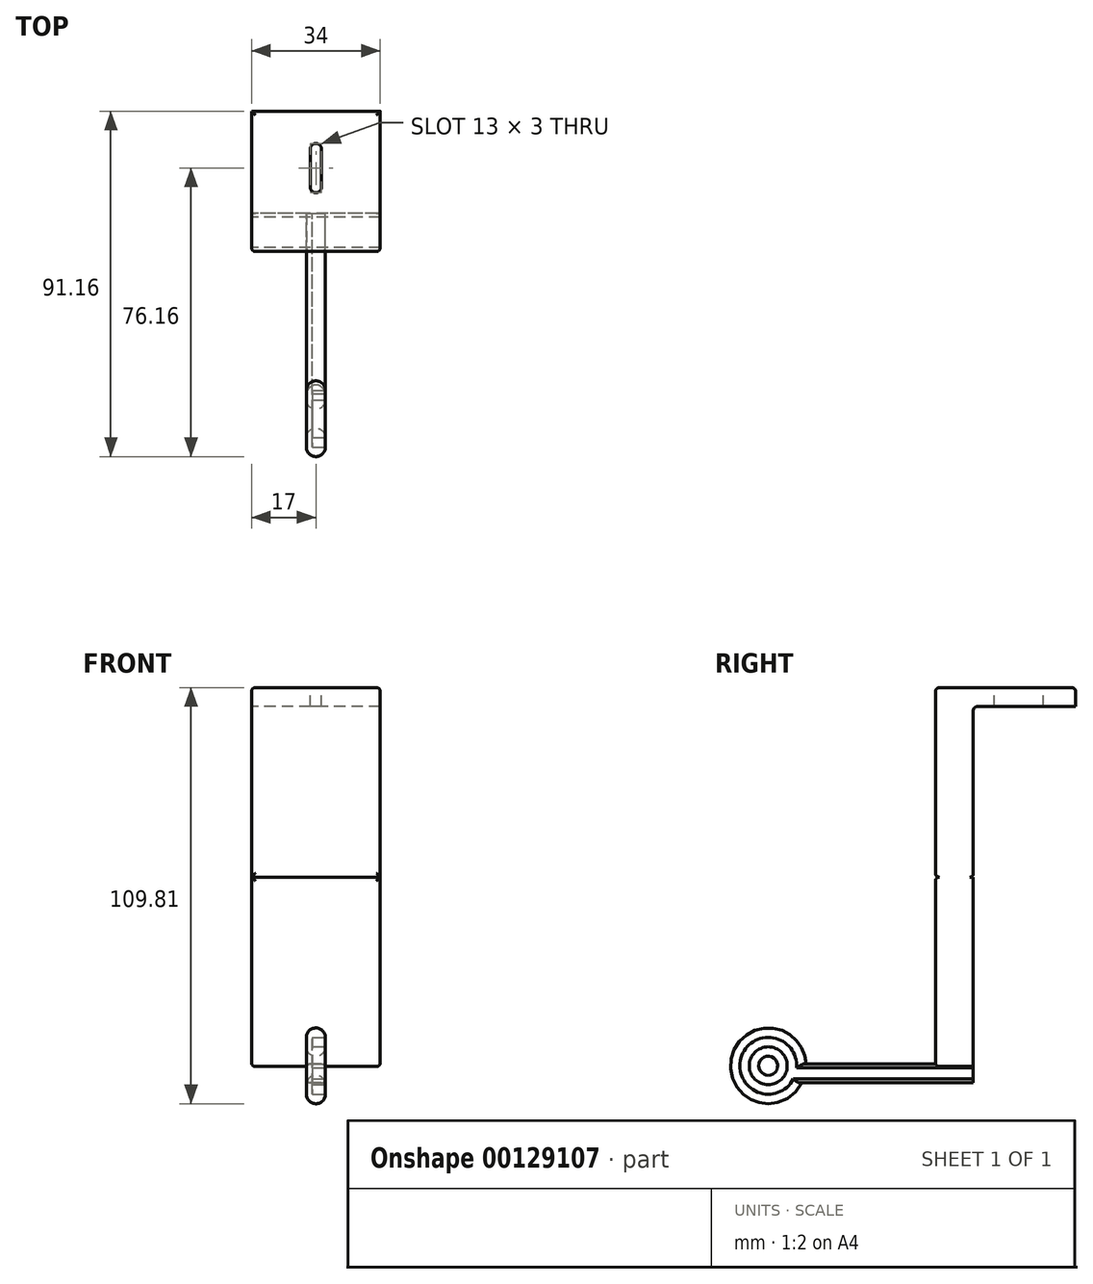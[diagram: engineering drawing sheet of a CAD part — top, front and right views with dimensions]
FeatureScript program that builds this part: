
annotation { "Feature Type Name" : "Feature", "Feature Type Description" : "" }
export const myFeature = defineFeature(function(context is Context, id is Id, definition is map)
    precondition{}
    {
        {
            var Q0;
            Q0=qCreatedBy(makeId("Right.planeOp"),FACE);
            var sketch = newSketch(context, id + "F0", { "sketchPlane" : qUnion([Q0])});
            skLineSegment(sketch, "E0", {"start": v(0, 50) * mm, "end": v(0, 0) * mm});
            skLineSegment(sketch, "E1", {"start": v(0, 0) * mm, "end": v(-10, 0) * mm});
            skLineSegment(sketch, "E2", {"start": v(-10, 0) * mm, "end": v(-10, 45) * mm});
            skLineSegment(sketch, "E3", {"start": v(0, 50) * mm, "end": v(27, 50) * mm});
            skLineSegment(sketch, "E4", {"start": v(27, 50) * mm, "end": v(27, 45) * mm});
            skLineSegment(sketch, "E5", {"start": v(27, 45) * mm, "end": v(0, 45) * mm});
            skLineSegment(sketch, "E6", {"start": v(-10, 45) * mm, "end": v(-10, 50) * mm});
            skLineSegment(sketch, "E7", {"start": v(0, 50) * mm, "end": v(-10, 50) * mm});
            skSolve(sketch);
        }
        {
            var Q0;
            Q0 = qSketchRegion(id + "F0", true);
            extrude(context, id + "F1", {"entities" : qUnion([Q0]), "endBound" : BoundingType.SYMMETRIC, "depth" : 34 * mm});
        }
        {
            var Q0;
            Q0=makeQuery(id+"F1.opExtrude","CAP_EDGE",EDGE,{"disambiguationData":[OSD([sQuery(id+"F0.wireOp",EDGE,"kGD8HcLu-JmXt-PA5V-rn9M-nTJb1uLwhhb4")])],"isStart":true});
            var Q1;
            Q1=makeQuery(id+"F1.opExtrude","SWEPT_EDGE",EDGE,{"disambiguationData":[OSD([sQuery(id+"F0.wireOp",EDGE,"kGD8HcLu-JmXt-PA5V-rn9M-nTJb1uLwhhb4"),sQuery(id+"F0.wireOp",EDGE,"E0")])]});
            var Q2;
            Q2=makeQuery(id+"F1.opExtrude","CAP_EDGE",EDGE,{"disambiguationData":[OSD([sQuery(id+"F0.wireOp",EDGE,"kGD8HcLu-JmXt-PA5V-rn9M-nTJb1uLwhhb4")])],"isStart":false});
            var Q3;
            Q3=makeQuery(id+"F1.opExtrude","SWEPT_EDGE",EDGE,{"disambiguationData":[OSD([sQuery(id+"F0.wireOp",EDGE,"kGD8HcLu-JmXt-PA5V-rn9M-nTJb1uLwhhb4"),sQuery(id+"F0.wireOp",EDGE,"xnDH0qCi-kUXw-gPrd-kgDC-GyTHQjH4Tpmb")])]});
            var Q4;
            Q4=makeQuery(id+"F1.opExtrude","SWEPT_EDGE",EDGE,{"disambiguationData":[OSD([sQuery(id+"F0.wireOp",EDGE,"dkW7WdI2-pFLL-zcu9-3AvS-6kcVhIOYi34H"),sQuery(id+"F0.wireOp",EDGE,"xnDH0qCi-kUXw-gPrd-kgDC-GyTHQjH4Tpmb")])]});
            var Q5;
            Q5=makeQuery(id+"F1.opExtrude","CAP_EDGE",EDGE,{"disambiguationData":[OSD([sQuery(id+"F0.wireOp",EDGE,"xnDH0qCi-kUXw-gPrd-kgDC-GyTHQjH4Tpmb")])],"isStart":false});
            var Q6;
            Q6=makeQuery(id+"F1.opExtrude","CAP_EDGE",EDGE,{"disambiguationData":[OSD([sQuery(id+"F0.wireOp",EDGE,"xnDH0qCi-kUXw-gPrd-kgDC-GyTHQjH4Tpmb")])],"isStart":true});
            var Q7;
            Q7=makeQuery(id+"F1.opExtrude","CAP_EDGE",EDGE,{"disambiguationData":[OSD([sQuery(id+"F0.wireOp",EDGE,"E2")])],"isStart":true});
            var Q8;
            Q8=makeQuery(id+"F1.opExtrude","CAP_EDGE",EDGE,{"disambiguationData":[OSD([sQuery(id+"F0.wireOp",EDGE,"E2")])],"isStart":false});
            var Q9;
            Q9=makeQuery(id+"F1.opExtrude","CAP_EDGE",EDGE,{"disambiguationData":[OSD([sQuery(id+"F0.wireOp",EDGE,"dkW7WdI2-pFLL-zcu9-3AvS-6kcVhIOYi34H")])],"isStart":false});
            var Q10;
            Q10=makeQuery(id+"F1.opExtrude","CAP_EDGE",EDGE,{"disambiguationData":[OSD([sQuery(id+"F0.wireOp",EDGE,"dkW7WdI2-pFLL-zcu9-3AvS-6kcVhIOYi34H")])],"isStart":true});
            var Q11;
            Q11=makeQuery(id+"F1.opExtrude","SWEPT_EDGE",EDGE,{"disambiguationData":[OSD([sQuery(id+"F0.wireOp",EDGE,"E2"),sQuery(id+"F0.wireOp",EDGE,"dkW7WdI2-pFLL-zcu9-3AvS-6kcVhIOYi34H")])]});
            fillet(context, id + "F2", {"entities" : qUnion([Q0, Q1, Q2, Q3, Q4, Q5, Q6, Q7, Q8, Q9, Q10, Q11]), "radius" : 1 * mm, "tangentPropagation" : true, "allowEdgeOverflow" : false});
        }
        {
            var Q0;
            Q0=makeQuery(id+"F1.opExtrude","SWEPT_FACE",FACE,{"disambiguationData":[OSD([sQuery(id+"F0.wireOp",EDGE,"E3"),sQuery(id+"F0.wireOp",EDGE,"E7")])]});
            fillet(context, id + "F3", {"entities" : qUnion([Q0]), "radius" : 1 * mm, "tangentPropagation" : true, "allowEdgeOverflow" : false});
        }
        {
            var Q0;
            Q0=qCreatedBy(makeId("Front.planeOp"),FACE);
            var sketch = newSketch(context, id + "F4", { "sketchPlane" : qUnion([Q0])});
            skLineSegment(sketch, "E8", {"start": v(0, 0) * mm, "end": v(0, -50) * mm});
            skLineSegment(sketch, "E9", {"start": v(0, -50) * mm, "end": v(-17, -50) * mm});
            skLineSegment(sketch, "E10", {"start": v(0, 0) * mm, "end": v(-17, 0) * mm});
            skLineSegment(sketch, "E11", {"start": v(-17, 0) * mm, "end": v(-17, -50) * mm});
            skSolve(sketch);
        }
        {
            var Q0;
            Q0=makeQuery(id+"F4.imprint","IMPRINT",FACE,{"disambiguationData":[TD([[makeQuery(id+"F4.imprint","IMPRINT",EDGE,{"derivedFrom":sQuery(id+"F4.wireOp",EDGE,"E8")}),-1.0]])]});
            extrude(context, id + "F5", {"entities" : qUnion([Q0]), "depth" : 10 * mm});
        }
        {
            var Q0;
            Q0=makeQuery(id+"F5.opExtrude","SWEPT_BODY",BODY,{"disambiguationData":[OSD([sQuery(id+"F4.wireOp",EDGE,"E8"),sQuery(id+"F4.wireOp",EDGE,"E9"),sQuery(id+"F4.wireOp",EDGE,"E10"),sQuery(id+"F4.wireOp",EDGE,"E11")])]});
            var Q1;
            Q1=qCreatedBy(makeId("Right.planeOp"),FACE);
            mirror(context, id + "F6", {"operationType" : NewBodyOperationType.ADD, "entities" : qUnion([Q0]), "mirrorPlane" : qUnion([Q1])});
        }
        {
            var Q0;
            Q0=makeQuery(id+"F5.opExtrude","CAP_EDGE",EDGE,{"disambiguationData":[OSD([sQuery(id+"F4.wireOp",EDGE,"E11")])],"isStart":false});
            var Q1;
            {var subQ0=makeQuery(id+"F5.opExtrude","CAP_EDGE",EDGE,{"disambiguationData":[OSD([sQuery(id+"F4.wireOp",EDGE,"E9")])],"isStart":false});Q1=makeQuery(id+"F6.boolean.opBoolean","MERGE",EDGE,{"derivedFrom":[subQ0,makeQuery(id+"F6.opPattern","COPY",EDGE,{"derivedFrom":subQ0,"instanceName":"1"})]});}
            var Q2;
            Q2=makeQuery(id+"F6.opPattern","COPY",EDGE,{"derivedFrom":makeQuery(id+"F5.opExtrude","CAP_EDGE",EDGE,{"disambiguationData":[OSD([sQuery(id+"F4.wireOp",EDGE,"E11")])],"isStart":false}),"instanceName":"1"});
            var Q3;
            {var subQ0=makeQuery(id+"F5.opExtrude","CAP_EDGE",EDGE,{"disambiguationData":[OSD([sQuery(id+"F4.wireOp",EDGE,"E10")])],"isStart":false});Q3=makeQuery(id+"F6.boolean.opBoolean","MERGE",EDGE,{"derivedFrom":[subQ0,makeQuery(id+"F6.opPattern","COPY",EDGE,{"derivedFrom":subQ0,"instanceName":"1"})]});}
            var Q4;
            Q4=makeQuery(id+"F6.opPattern","COPY",EDGE,{"derivedFrom":makeQuery(id+"F5.opExtrude","SWEPT_EDGE",EDGE,{"disambiguationData":[OSD([sQuery(id+"F4.wireOp",EDGE,"E9"),sQuery(id+"F4.wireOp",EDGE,"E11")])]}),"instanceName":"1"});
            var Q5;
            Q5=makeQuery(id+"F5.opExtrude","SWEPT_EDGE",EDGE,{"disambiguationData":[OSD([sQuery(id+"F4.wireOp",EDGE,"E9"),sQuery(id+"F4.wireOp",EDGE,"E11")])]});
            fillet(context, id + "F7", {"entities" : qUnion([Q0, Q1, Q2, Q3, Q4, Q5]), "radius" : 1 * mm, "tangentPropagation" : true, "allowEdgeOverflow" : false});
        }
        {
            var Q0;
            Q0=qCreatedBy(makeId("Front.planeOp"),FACE);
            var sketch = newSketch(context, id + "F8", { "sketchPlane" : qUnion([Q0])});
            skLineSegment(sketch, "E12.bottom", {"start": v(0, -49.32) * mm, "end": v(2.5, -49.32) * mm});
            skLineSegment(sketch, "E12.top", {"start": v(0, -54.32) * mm, "end": v(2.5, -54.32) * mm});
            skLineSegment(sketch, "E12.left", {"start": v(0, -49.32) * mm, "end": v(0, -54.32) * mm});
            skLineSegment(sketch, "E12.right", {"start": v(2.5, -49.32) * mm, "end": v(2.5, -54.32) * mm});
            skLineSegment(sketch, "E13.MirrorCS", {"start": v(-2.5, -49.32) * mm, "end": v(-2.5, -54.32) * mm});
            skLineSegment(sketch, "E14.MirrorCS", {"start": v(0, -54.32) * mm, "end": v(-2.5, -54.32) * mm});
            skLineSegment(sketch, "E15.MirrorCS", {"start": v(0, -49.32) * mm, "end": v(-2.5, -49.32) * mm});
            skSolve(sketch);
        }
        {
            var Q0;
            Q0 = qSketchRegion(id + "F8", true);
            extrude(context, id + "F9", {"entities" : qUnion([Q0]), "operationType" : NewBodyOperationType.ADD, "depth" : 50 * mm});
        }
        {
            var Q0;
            Q0=makeQuery(id+"F9.opExtrude","SWEPT_EDGE",EDGE,{"disambiguationData":[OSD([sQuery(id+"F8.wireOp",EDGE,"E13.MirrorCS"),sQuery(id+"F8.wireOp",EDGE,"E14.MirrorCS")])]});
            var Q1;
            Q1=makeQuery(id+"F9.opExtrude","CAP_EDGE",EDGE,{"disambiguationData":[OSD([sQuery(id+"F8.wireOp",EDGE,"E12.top"),sQuery(id+"F8.wireOp",EDGE,"E14.MirrorCS")])],"isStart":false});
            var Q2;
            Q2=makeQuery(id+"F9.opExtrude","SWEPT_EDGE",EDGE,{"disambiguationData":[OSD([sQuery(id+"F8.wireOp",EDGE,"E12.top"),sQuery(id+"F8.wireOp",EDGE,"E12.right")])]});
            var Q3;
            Q3=makeQuery(id+"F9.opExtrude","SWEPT_EDGE",EDGE,{"disambiguationData":[OSD([sQuery(id+"F8.wireOp",EDGE,"E12.bottom"),sQuery(id+"F8.wireOp",EDGE,"E12.right")])]});
            var Q4;
            Q4=makeQuery(id+"F9.opExtrude","CAP_EDGE",EDGE,{"disambiguationData":[OSD([sQuery(id+"F8.wireOp",EDGE,"E12.bottom"),sQuery(id+"F8.wireOp",EDGE,"E15.MirrorCS")])],"isStart":false});
            var Q5;
            Q5=makeQuery(id+"F9.opExtrude","SWEPT_EDGE",EDGE,{"disambiguationData":[OSD([sQuery(id+"F8.wireOp",EDGE,"E13.MirrorCS"),sQuery(id+"F8.wireOp",EDGE,"E15.MirrorCS")])]});
            fillet(context, id + "F10", {"entities" : qUnion([Q0, Q1, Q2, Q3, Q4, Q5]), "radius" : 1 * mm, "tangentPropagation" : true, "allowEdgeOverflow" : false});
        }
        {
            var Q0;
            Q0=qCreatedBy(makeId("Right.planeOp"),FACE);
            var sketch = newSketch(context, id + "F11", { "sketchPlane" : qUnion([Q0])});
            skCircle(sketch, "E16", {"center": v(-54.16, -49.8) * mm, "radius": 10 * mm});
            skCircle(sketch, "E17", {"center": v(-54.16, -49.8) * mm, "radius": 2.5 * mm});
            skLineSegment(sketch, "E18", {"start": v(-54, -39.8) * mm, "end": v(-54, -47.31) * mm});
            skSolve(sketch);
        }
        {
            var Q0;
            Q0=makeQuery(id+"F11.imprint","IMPRINT",FACE,{"disambiguationData":[TD([[makeQuery(id+"F11.imprint","IMPRINT",EDGE,{"derivedFrom":sQuery(id+"F11.wireOp",EDGE,"E16")}),1.0]])]});
            extrude(context, id + "F12", {"entities" : qUnion([Q0]), "operationType" : NewBodyOperationType.ADD, "endBound" : BoundingType.SYMMETRIC, "depth" : 5 * mm});
        }
        {
            var Q0;
            Q0=makeQuery(id+"F12.opExtrude","CAP_EDGE",EDGE,{"disambiguationData":[OSD([sQuery(id+"F11.wireOp",EDGE,"E17")])],"isStart":true});
            var Q1;
            Q1=makeQuery(id+"F12.opExtrude","CAP_EDGE",EDGE,{"disambiguationData":[OSD([sQuery(id+"F11.wireOp",EDGE,"E17")])],"isStart":false});
            fillet(context, id + "F13", {"entities" : qUnion([Q0, Q1]), "radius" : 2.5 * mm, "tangentPropagation" : true, "allowEdgeOverflow" : false});
        }
        {
            var Q0;
            Q0=makeQuery(id+"F12.opExtrude","CAP_EDGE",EDGE,{"disambiguationData":[OSD([sQuery(id+"F11.wireOp",EDGE,"E16")])],"isStart":false});
            var Q1;
            Q1=makeQuery(id+"F12.opExtrude","CAP_EDGE",EDGE,{"disambiguationData":[OSD([sQuery(id+"F11.wireOp",EDGE,"E16")])],"isStart":true});
            fillet(context, id + "F14", {"entities" : qUnion([Q0, Q1]), "radius" : 2.5 * mm, "tangentPropagation" : true, "allowEdgeOverflow" : false});
        }
        {
            var Q0;
            Q0=makeQuery(id+"F1.opExtrude","SWEPT_FACE",FACE,{"disambiguationData":[OSD([sQuery(id+"F0.wireOp",EDGE,"E3"),sQuery(id+"F0.wireOp",EDGE,"E7")])]});
            var sketch = newSketch(context, id + "F15", { "sketchPlane" : qUnion([Q0])});
            skLineSegment(sketch, "E19", {"start": v(16, 0) * mm, "end": v(-16, 0) * mm});
            skLineSegment(sketch, "E20", {"start": v(-16, 0) * mm, "end": v(-16, 26) * mm});
            skLineSegment(sketch, "E21", {"start": v(-16, 26) * mm, "end": v(46.33, 26) * mm});
            skLineSegment(sketch, "E22", {"start": v(16, 26) * mm, "end": v(16, 0) * mm});
            skPoint(sketch, "E23.positionSnap0", {"position": v(-16, 8.5) * mm});
            skSolve(sketch);
        }
        {
            var Q0;
            Q0=makeQuery(id+"F15.imprint","IMPRINT",FACE,{"disambiguationData":[TD([[makeQuery(id+"F15.imprint","IMPRINT",EDGE,{"derivedFrom":sQuery(id+"F15.wireOp",EDGE,"E19")}),-1.0]])]});
            var sketch = newSketch(context, id + "F16", { "sketchPlane" : qUnion([Q0])});
            skPoint(sketch, "E24", {"position": v(0, 7) * mm});
            skPoint(sketch, "E25", {"position": v(0, 24.92) * mm});
            skPoint(sketch, "E26", {"position": v(0, 17) * mm});
            skCircle(sketch, "E27", {"center": v(0, 7) * mm, "radius": 1.5 * mm});
            skCircle(sketch, "E28", {"center": v(0, 17) * mm, "radius": 1.5 * mm});
            skLineSegment(sketch, "E29", {"start": v(1.5, 7) * mm, "end": v(1.5, 17) * mm});
            skLineSegment(sketch, "E30", {"start": v(-1.5, 7) * mm, "end": v(-1.5, 17) * mm});
            skSolve(sketch);
        }
        {
            var Q0;
            Q0 = qSketchRegion(id + "F16", true);
            extrude(context, id + "F17", {"entities" : qUnion([Q0]), "operationType" : NewBodyOperationType.REMOVE, "oppositeDirection" : true, "depth" : 5.5 * mm});
        }
        {
            var Q0;
            Q0=makeQuery(id+"F12.opExtrude","CAP_FACE",FACE,{"disambiguationData":[OSD([sQuery(id+"F11.wireOp",EDGE,"E16"),sQuery(id+"F11.wireOp",EDGE,"E17")])],"isStart":false});
            extrude(context, id + "F18", {"entities" : qUnion([Q0]), "operationType" : NewBodyOperationType.REMOVE, "oppositeDirection" : true, "depth" : 3.5 * mm});
        }
    });
